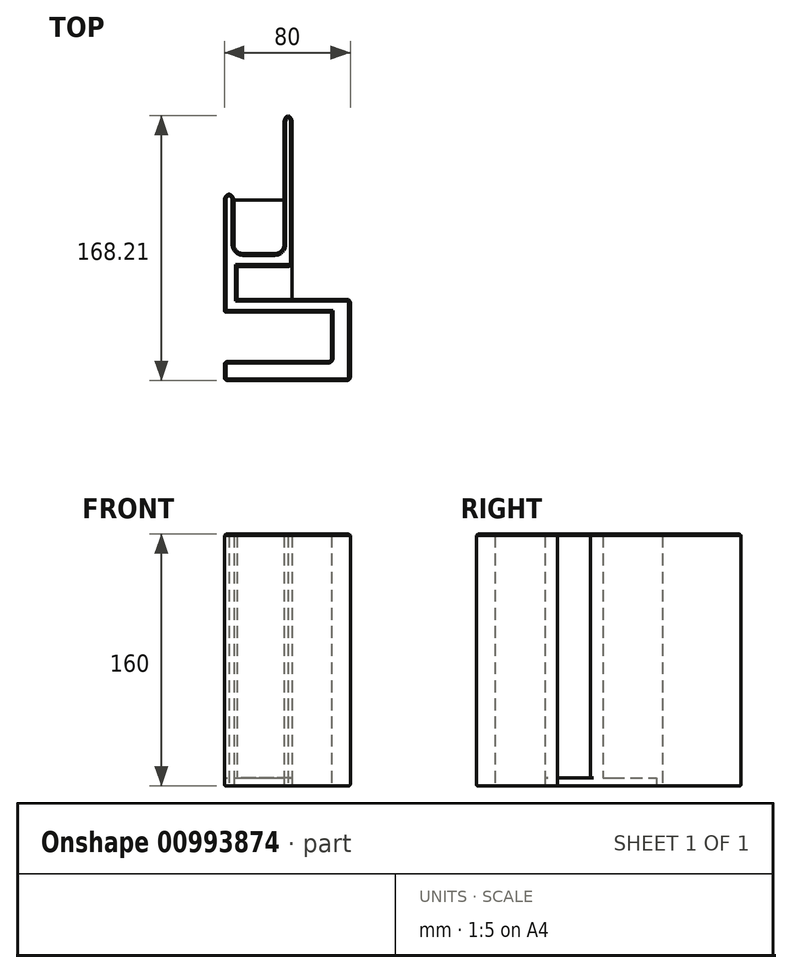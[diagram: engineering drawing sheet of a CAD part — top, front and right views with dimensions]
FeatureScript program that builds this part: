
annotation { "Feature Type Name" : "Feature", "Feature Type Description" : "" }
export const myFeature = defineFeature(function(context is Context, id is Id, definition is map)
    precondition{}
    {
        {
            var Q0;
            Q0=qCreatedBy(makeId("Top.planeOp"),FACE);
            var sketch = newSketch(context, id + "F0", { "sketchPlane" : qUnion([Q0])});
            skLineSegment(sketch, "E0.left", {"start": v(0, 0) * mm, "end": v(0, 90) * mm});
            skLineSegment(sketch, "E0.right", {"start": v(-32, 0) * mm, "end": v(-32, 40) * mm});
            skLineSegment(sketch, "E1.bottom", {"start": v(0, 90) * mm, "end": v(5, 90) * mm});
            skLineSegment(sketch, "E1.left", {"start": v(0, 90) * mm, "end": v(0, 0) * mm});
            skLineSegment(sketch, "E1.right", {"start": v(5, 90) * mm, "end": v(5, 0) * mm});
            skLineSegment(sketch, "E2.bottom", {"start": v(-32, 40) * mm, "end": v(-38, 40) * mm});
            skLineSegment(sketch, "E2.right", {"start": v(-38, 40) * mm, "end": v(-38, 0) * mm});
            skLineSegment(sketch, "E3.top", {"start": v(-38, 2) * mm, "end": v(5, 2) * mm});
            skLineSegment(sketch, "E3.left", {"start": v(-38, 0) * mm, "end": v(-38, 2) * mm});
            skLineSegment(sketch, "E3.right", {"start": v(5, 0) * mm, "end": v(5, 2) * mm});
            skLineSegment(sketch, "E4", {"start": v(-38, 0) * mm, "end": v(5, 0) * mm});
            skSolve(sketch);
        }
        {
            var Q0;
            {var subQ3=sQuery(id+"F0.wireOp",EDGE,"E1.bottom");Q0=makeQuery(id+"F0.imprint","IMPRINT",FACE,{"disambiguationData":[TD([[makeQuery(id+"F0.imprint","IMPRINT",EDGE,{"derivedFrom":subQ3}),-1.0]])]});}
            var Q1;
            {var subQ3=sQuery(id+"F0.wireOp",EDGE,"E2.bottom");Q1=makeQuery(id+"F0.imprint","IMPRINT",FACE,{"disambiguationData":[TD([[makeQuery(id+"F0.imprint","IMPRINT",EDGE,{"derivedFrom":subQ3}),1.0]])]});}
            var Q2;
            {var subQ0=sQuery(id+"F0.wireOp",EDGE,"E3.top");var subQ1=sQuery(id+"F0.wireOp",EDGE,"E0.right");var subQ2=makeQuery(id+"F0.imprint","INTERSECT",VERTEX,{"derivedFrom":[subQ1,subQ0]});Q2=makeQuery(id+"F0.imprint","IMPRINT",FACE,{"disambiguationData":[TD([[makeQuery(id+"F0.imprint","IMPRINT",EDGE,{"disambiguationData":[TD([[subQ2,1.0]])],"derivedFrom":subQ1}),1.0]])]});}
            var Q3;
            {var subQ0=sQuery(id+"F0.wireOp",EDGE,"E3.top");var subQ1=sQuery(id+"F0.wireOp",EDGE,"E0.left");var subQ2=makeQuery(id+"F0.imprint","INTERSECT",VERTEX,{"derivedFrom":[subQ1,subQ0]});Q3=makeQuery(id+"F0.imprint","IMPRINT",FACE,{"disambiguationData":[TD([[makeQuery(id+"F0.imprint","IMPRINT",EDGE,{"disambiguationData":[TD([[subQ2,1.0]])],"derivedFrom":subQ1}),1.0]])]});}
            var Q4;
            {var subQ0=sQuery(id+"F0.wireOp",EDGE,"E3.top");var subQ1=sQuery(id+"F0.wireOp",EDGE,"E0.left");var subQ2=makeQuery(id+"F0.imprint","INTERSECT",VERTEX,{"derivedFrom":[subQ1,subQ0]});Q4=makeQuery(id+"F0.imprint","IMPRINT",FACE,{"disambiguationData":[TD([[makeQuery(id+"F0.imprint","IMPRINT",EDGE,{"disambiguationData":[TD([[subQ2,1.0]])],"derivedFrom":subQ1}),-1.0]])]});}
            extrude(context, id + "F1", {"entities" : qUnion([Q0, Q1, Q2, Q3, Q4]), "depth" : 160 * mm, "offsetDistance" : 25 * mm});
        }
        {
            var Q0;
            Q0=makeQuery(id+"F1.opExtrude","CAP_FACE",FACE,{"disambiguationData":[OSD([sQuery(id+"F0.wireOp",EDGE,"E0.left"),sQuery(id+"F0.wireOp",EDGE,"E0.right"),sQuery(id+"F0.wireOp",EDGE,"E1.bottom"),sQuery(id+"F0.wireOp",EDGE,"E1.right"),sQuery(id+"F0.wireOp",EDGE,"E2.bottom"),sQuery(id+"F0.wireOp",EDGE,"E2.right"),sQuery(id+"F0.wireOp",EDGE,"E3.top"),sQuery(id+"F0.wireOp",EDGE,"E4")])],"isStart":true});
            var sketch = newSketch(context, id + "F2", { "sketchPlane" : qUnion([Q0])});
            skLineSegment(sketch, "E5.bottom", {"start": v(-38, 0) * mm, "end": v(5, 0) * mm});
            skLineSegment(sketch, "E5.top", {"start": v(-38, 35) * mm, "end": v(5, 35) * mm});
            skLineSegment(sketch, "E5.left", {"start": v(-38, 0) * mm, "end": v(-38, 35) * mm});
            skLineSegment(sketch, "E5.right", {"start": v(5, 0) * mm, "end": v(5, 35) * mm});
            skSolve(sketch);
        }
        {
            var Q0;
            Q0 = qSketchRegion(id + "F2", true);
            extrude(context, id + "F3", {"entities" : qUnion([Q0]), "oppositeDirection" : true, "depth" : 160 * mm, "offsetDistance" : 25 * mm});
        }
        {
            var Q0;
            Q0=makeQuery(id+"F1.opExtrude","SWEPT_EDGE",EDGE,{"disambiguationData":[OSD([sQuery(id+"F0.wireOp",EDGE,"E0.right"),sQuery(id+"F0.wireOp",EDGE,"E2.bottom")])]});
            var Q1;
            Q1=makeQuery(id+"F1.opExtrude","SWEPT_EDGE",EDGE,{"disambiguationData":[OSD([sQuery(id+"F0.wireOp",EDGE,"E0.left"),sQuery(id+"F0.wireOp",EDGE,"E1.bottom")])]});
            var Q2;
            Q2=makeQuery(id+"F1.opExtrude","SWEPT_EDGE",EDGE,{"disambiguationData":[OSD([sQuery(id+"F0.wireOp",EDGE,"E2.bottom"),sQuery(id+"F0.wireOp",EDGE,"E2.right")])]});
            var Q3;
            Q3=makeQuery(id+"F1.opExtrude","SWEPT_EDGE",EDGE,{"disambiguationData":[OSD([sQuery(id+"F0.wireOp",EDGE,"E1.bottom"),sQuery(id+"F0.wireOp",EDGE,"E1.right")])]});
            fillet(context, id + "F4", {"entities" : qUnion([Q0, Q1, Q2, Q3]), "radius" : 4 * mm, "tangentPropagation" : true, "allowEdgeOverflow" : false});
        }
        {
            var Q0;
            Q0=makeQuery(id+"F1.opExtrude","SWEPT_EDGE",EDGE,{"disambiguationData":[OSD([sQuery(id+"F0.wireOp",EDGE,"E0.right"),sQuery(id+"F0.wireOp",EDGE,"E3.top")])]});
            var Q1;
            Q1=makeQuery(id+"F1.opExtrude","SWEPT_EDGE",EDGE,{"disambiguationData":[OSD([sQuery(id+"F0.wireOp",EDGE,"E0.left"),sQuery(id+"F0.wireOp",EDGE,"E3.top")])]});
            fillet(context, id + "F5", {"entities" : qUnion([Q0, Q1]), "radius" : 6 * mm, "tangentPropagation" : true, "allowEdgeOverflow" : false});
        }
        {
            var Q0;
            Q0=qCreatedBy(makeId("Top.planeOp"),FACE);
            var sketch = newSketch(context, id + "F6", { "sketchPlane" : qUnion([Q0])});
            skLineSegment(sketch, "E6.bottom", {"start": v(28, -6) * mm, "end": v(-30, -6) * mm});
            skLineSegment(sketch, "E6.top", {"start": v(28, -27) * mm, "end": v(-30, -27) * mm});
            skLineSegment(sketch, "E6.left", {"start": v(28, -6) * mm, "end": v(28, -27) * mm});
            skLineSegment(sketch, "E6.right", {"start": v(-30, -6) * mm, "end": v(-30, -27) * mm});
            skSolve(sketch);
        }
        {
            var Q0;
            Q0=makeQuery(id+"F6.imprint","IMPRINT",FACE,{"disambiguationData":[TD([[makeQuery(id+"F6.imprint","IMPRINT",EDGE,{"derivedFrom":sQuery(id+"F6.wireOp",EDGE,"E6.bottom")}),1.0]])]});
            extrude(context, id + "F7", {"entities" : qUnion([Q0]), "operationType" : NewBodyOperationType.REMOVE, "depth" : 250 * mm, "offsetDistance" : 25 * mm});
        }
        {
            var Q0;
            Q0=qCreatedBy(makeId("Top.planeOp"),FACE);
            var sketch = newSketch(context, id + "F8", { "sketchPlane" : qUnion([Q0])});
            skLineSegment(sketch, "E7.bottom", {"start": v(-38, -35) * mm, "end": v(5, -35) * mm});
            skLineSegment(sketch, "E7.top", {"start": v(-38, 36) * mm, "end": v(5, 36) * mm});
            skLineSegment(sketch, "E7.left", {"start": v(-38, -35) * mm, "end": v(-38, 36) * mm});
            skLineSegment(sketch, "E7.right", {"start": v(5, -35) * mm, "end": v(5, 36) * mm});
            skSolve(sketch);
        }
        {
            var Q0;
            Q0=makeQuery(id+"F8.imprint","IMPRINT",FACE,{"disambiguationData":[TD([[makeQuery(id+"F8.imprint","IMPRINT",EDGE,{"derivedFrom":sQuery(id+"F8.wireOp",EDGE,"E7.bottom")}),1.0]])]});
            extrude(context, id + "F9", {"entities" : qUnion([Q0]), "depth" : 5 * mm, "offsetDistance" : 25 * mm});
        }
        {
            var Q0;
            Q0=makeQuery(id+"F9.opExtrude","SWEPT_EDGE",EDGE,{"disambiguationData":[OSD([sQuery(id+"F8.wireOp",EDGE,"E7.top"),sQuery(id+"F8.wireOp",EDGE,"E7.left")])]});
            fillet(context, id + "F10", {"entities" : qUnion([Q0]), "radius" : 4 * mm, "tangentPropagation" : true, "allowEdgeOverflow" : false});
        }
        {
            var Q0;
            {var subQ0=sQuery(id+"F2.wireOp",EDGE,"E5.right");var subQ2=sQuery(id+"F2.wireOp",EDGE,"E5.top");Q0=makeQuery(id+"F7.boolean.opBoolean","SPLIT",FACE,{"disambiguationData":[TD([makeQuery(id+"F3.opExtrude","SWEPT_FACE",FACE,{"disambiguationData":[OSD([subQ2])]})])],"derivedFrom":makeQuery(id+"F3.opExtrude","SWEPT_FACE",FACE,{"disambiguationData":[OSD([subQ0])]})});}
            extrude(context, id + "F11", {"entities" : qUnion([Q0]), "depth" : 25 * mm, "offsetDistance" : 25 * mm});
        }
        {
            var Q0;
            Q0=qCreatedBy(makeId("Top.planeOp"),FACE);
            var sketch = newSketch(context, id + "F12", { "sketchPlane" : qUnion([Q0])});
            skLineSegment(sketch, "E8", {"start": v(30, -27.01) * mm, "end": v(42, -27.01) * mm});
            skLineSegment(sketch, "E9", {"start": v(42, -27.01) * mm, "end": v(42, -78.5) * mm});
            skLineSegment(sketch, "E10", {"start": v(42, -78.5) * mm, "end": v(-38, -78.5) * mm});
            skLineSegment(sketch, "E11", {"start": v(-38, -78.5) * mm, "end": v(-38, -66.5) * mm});
            skLineSegment(sketch, "E12", {"start": v(-38, -66.5) * mm, "end": v(30, -66.5) * mm});
            skLineSegment(sketch, "E13", {"start": v(30, -66.5) * mm, "end": v(30, -27.01) * mm});
            skSolve(sketch);
        }
        {
            var Q0;
            Q0=makeQuery(id+"F12.imprint","IMPRINT",FACE,{"disambiguationData":[TD([[makeQuery(id+"F12.imprint","IMPRINT",EDGE,{"derivedFrom":sQuery(id+"F12.wireOp",EDGE,"E8")}),-1.0]])]});
            extrude(context, id + "F13", {"entities" : qUnion([Q0]), "operationType" : NewBodyOperationType.ADD, "depth" : 160 * mm, "offsetDistance" : 25 * mm});
        }
        {
            var Q0;
            Q0=makeQuery(id+"F11.opExtrude","CAP_EDGE",EDGE,{"disambiguationData":[OSD([sQuery(id+"F2.wireOp",EDGE,"E5.top"),sQuery(id+"F2.wireOp",EDGE,"E5.right")])],"isStart":false});
            var Q1;
            Q1=makeQuery(id+"F13.opExtrude","SWEPT_EDGE",EDGE,{"disambiguationData":[OSD([sQuery(id+"F12.wireOp",EDGE,"E12"),sQuery(id+"F12.wireOp",EDGE,"E13")])]});
            var Q2;
            Q2=makeQuery(id+"F13.opExtrude","SWEPT_EDGE",EDGE,{"disambiguationData":[OSD([sQuery(id+"F12.wireOp",EDGE,"E8"),sQuery(id+"F12.wireOp",EDGE,"E9")])]});
            var Q3;
            Q3=makeQuery(id+"F13.opExtrude","SWEPT_EDGE",EDGE,{"disambiguationData":[OSD([sQuery(id+"F12.wireOp",EDGE,"E9"),sQuery(id+"F12.wireOp",EDGE,"E10")])]});
            var Q4;
            Q4=makeQuery(id+"F3.opExtrude","SWEPT_EDGE",EDGE,{"disambiguationData":[OSD([sQuery(id+"F2.wireOp",EDGE,"E5.top"),sQuery(id+"F2.wireOp",EDGE,"E5.left")])]});
            var Q5;
            Q5=makeQuery(id+"F13.opExtrude","SWEPT_EDGE",EDGE,{"disambiguationData":[OSD([sQuery(id+"F12.wireOp",EDGE,"E10"),sQuery(id+"F12.wireOp",EDGE,"E11")])]});
            var Q6;
            Q6=makeQuery(id+"F13.opExtrude","SWEPT_EDGE",EDGE,{"disambiguationData":[OSD([sQuery(id+"F12.wireOp",EDGE,"E11"),sQuery(id+"F12.wireOp",EDGE,"E12")])]});
            var Q7;
            Q7=makeQuery(id+"F7.boolean.opBoolean","INTERSECT",EDGE,{"derivedFrom":[makeQuery(id+"F3.opExtrude","SWEPT_FACE",FACE,{"disambiguationData":[OSD([sQuery(id+"F2.wireOp",EDGE,"E5.right")])]}),makeQuery(id+"F7.opExtrude","SWEPT_FACE",FACE,{"disambiguationData":[OSD([sQuery(id+"F6.wireOp",EDGE,"E6.bottom")])]})]});
            fillet(context, id + "F14", {"entities" : qUnion([Q0, Q1, Q2, Q3, Q4, Q5, Q6, Q7]), "radius" : 2 * mm, "tangentPropagation" : true, "allowEdgeOverflow" : false});
        }
        {
            var Q0;
            Q0=makeQuery(id+"F3.opExtrude","SWEPT_BODY",BODY,{"disambiguationData":[OSD([sQuery(id+"F2.wireOp",EDGE,"E5.bottom"),sQuery(id+"F2.wireOp",EDGE,"E5.top"),sQuery(id+"F2.wireOp",EDGE,"E5.left"),sQuery(id+"F2.wireOp",EDGE,"E5.right")])]});
            var Q1;
            Q1=makeQuery(id+"F11.opExtrude","SWEPT_BODY",BODY,{"disambiguationData":[OSD([sQuery(id+"F2.wireOp",EDGE,"E5.right")])]});
            var Q2;
            Q2=makeQuery(id+"F1.opExtrude","SWEPT_BODY",BODY,{"disambiguationData":[OSD([sQuery(id+"F0.wireOp",EDGE,"E0.left"),sQuery(id+"F0.wireOp",EDGE,"E0.right"),sQuery(id+"F0.wireOp",EDGE,"E1.bottom"),sQuery(id+"F0.wireOp",EDGE,"E1.right"),sQuery(id+"F0.wireOp",EDGE,"E2.bottom"),sQuery(id+"F0.wireOp",EDGE,"E2.right"),sQuery(id+"F0.wireOp",EDGE,"E3.top"),sQuery(id+"F0.wireOp",EDGE,"E4")])]});
            var Q3;
            Q3=makeQuery(id+"F9.opExtrude","SWEPT_BODY",BODY,{"disambiguationData":[OSD([sQuery(id+"F8.wireOp",EDGE,"E7.bottom"),sQuery(id+"F8.wireOp",EDGE,"E7.top"),sQuery(id+"F8.wireOp",EDGE,"E7.left"),sQuery(id+"F8.wireOp",EDGE,"E7.right")])]});
            booleanBodies(context, id + "F15", {"operationType" : BooleanOperationType.UNION, "tools" : qUnion([Q0, Q1, Q2, Q3])});
        }
        {
            var Q0;
            {var subQ0=sQuery(id+"F2.wireOp",EDGE,"E5.right");var subQ1=sQuery(id+"F2.wireOp",EDGE,"E5.top");var subQ2=makeQuery(id+"F3.opExtrude","CAP_FACE",FACE,{"disambiguationData":[OSD([sQuery(id+"F2.wireOp",EDGE,"E5.bottom"),subQ1,sQuery(id+"F2.wireOp",EDGE,"E5.left"),subQ0])],"isStart":false});Q0=makeQuery(id+"F15.opBoolean","MERGE",FACE,{"derivedFrom":[makeQuery(id+"F1.opExtrude","CAP_FACE",FACE,{"disambiguationData":[OSD([sQuery(id+"F0.wireOp",EDGE,"E0.left"),sQuery(id+"F0.wireOp",EDGE,"E0.right"),sQuery(id+"F0.wireOp",EDGE,"E1.bottom"),sQuery(id+"F0.wireOp",EDGE,"E1.right"),sQuery(id+"F0.wireOp",EDGE,"E2.bottom"),sQuery(id+"F0.wireOp",EDGE,"E2.right"),sQuery(id+"F0.wireOp",EDGE,"E3.top"),sQuery(id+"F0.wireOp",EDGE,"E4")])],"isStart":false}),subQ2,makeQuery(id+"F13.boolean.opBoolean","MERGE",FACE,{"derivedFrom":[makeQuery(id+"F11.opExtrude","SWEPT_FACE",FACE,{"disambiguationData":[OSD([subQ0]),TDD([makeQuery(id+"F7.boolean.opBoolean","SPLIT",EDGE,{"disambiguationData":[TD([makeQuery(id+"F3.opExtrude","SWEPT_FACE",FACE,{"disambiguationData":[OSD([subQ1])]})])],"derivedFrom":makeQuery(id+"F3.opExtrude","CAP_EDGE",EDGE,{"disambiguationData":[OSD([subQ0])],"isStart":false})})])]}),makeQuery(id+"F13.opExtrude","CAP_FACE",FACE,{"disambiguationData":[OSD([sQuery(id+"F12.wireOp",EDGE,"E8"),sQuery(id+"F12.wireOp",EDGE,"E9"),sQuery(id+"F12.wireOp",EDGE,"E10"),sQuery(id+"F12.wireOp",EDGE,"E11"),sQuery(id+"F12.wireOp",EDGE,"E12"),sQuery(id+"F12.wireOp",EDGE,"E13")])],"isStart":false})]})]});}
            chamfer(context, id + "F16", {"entities" : qUnion([Q0]), "width" : 1 * mm, "tangentPropagation" : true});
        }
        {
            var Q0;
            {var subQ0=sQuery(id+"F2.wireOp",EDGE,"E5.right");var subQ1=sQuery(id+"F2.wireOp",EDGE,"E5.top");var subQ2=makeQuery(id+"F3.opExtrude","CAP_FACE",FACE,{"disambiguationData":[OSD([sQuery(id+"F2.wireOp",EDGE,"E5.bottom"),subQ1,sQuery(id+"F2.wireOp",EDGE,"E5.left"),subQ0])],"isStart":true});Q0=makeQuery(id+"F15.opBoolean","MERGE",FACE,{"derivedFrom":[makeQuery(id+"F1.opExtrude","CAP_FACE",FACE,{"disambiguationData":[OSD([sQuery(id+"F0.wireOp",EDGE,"E0.left"),sQuery(id+"F0.wireOp",EDGE,"E0.right"),sQuery(id+"F0.wireOp",EDGE,"E1.bottom"),sQuery(id+"F0.wireOp",EDGE,"E1.right"),sQuery(id+"F0.wireOp",EDGE,"E2.bottom"),sQuery(id+"F0.wireOp",EDGE,"E2.right"),sQuery(id+"F0.wireOp",EDGE,"E3.top"),sQuery(id+"F0.wireOp",EDGE,"E4")])],"isStart":true}),makeQuery(id+"F9.opExtrude","CAP_FACE",FACE,{"disambiguationData":[OSD([sQuery(id+"F8.wireOp",EDGE,"E7.bottom"),sQuery(id+"F8.wireOp",EDGE,"E7.top"),sQuery(id+"F8.wireOp",EDGE,"E7.left"),sQuery(id+"F8.wireOp",EDGE,"E7.right")])],"isStart":true}),subQ2,makeQuery(id+"F13.boolean.opBoolean","MERGE",FACE,{"derivedFrom":[makeQuery(id+"F11.opExtrude","SWEPT_FACE",FACE,{"disambiguationData":[OSD([subQ0]),TDD([makeQuery(id+"F7.boolean.opBoolean","SPLIT",EDGE,{"disambiguationData":[TD([makeQuery(id+"F3.opExtrude","SWEPT_FACE",FACE,{"disambiguationData":[OSD([subQ1])]})])],"derivedFrom":makeQuery(id+"F3.opExtrude","CAP_EDGE",EDGE,{"disambiguationData":[OSD([subQ0])],"isStart":true})})])]}),makeQuery(id+"F13.opExtrude","CAP_FACE",FACE,{"disambiguationData":[OSD([sQuery(id+"F12.wireOp",EDGE,"E8"),sQuery(id+"F12.wireOp",EDGE,"E9"),sQuery(id+"F12.wireOp",EDGE,"E10"),sQuery(id+"F12.wireOp",EDGE,"E11"),sQuery(id+"F12.wireOp",EDGE,"E12"),sQuery(id+"F12.wireOp",EDGE,"E13")])],"isStart":true})]})]});}
            var Q1;
            Q1=makeQuery(id+"F9.opExtrude","SWEPT_EDGE",EDGE,{"disambiguationData":[OSD([sQuery(id+"F8.wireOp",EDGE,"E7.bottom"),sQuery(id+"F8.wireOp",EDGE,"E7.left")])]});
            fillet(context, id + "F17", {"entities" : qUnion([Q0, Q1]), "tangentPropagation" : true, "radius" : 1 * mm, "defaultsChanged" : false, "vertexSettings" : [], "allowEdgeOverflow" : false});
        }
    });
